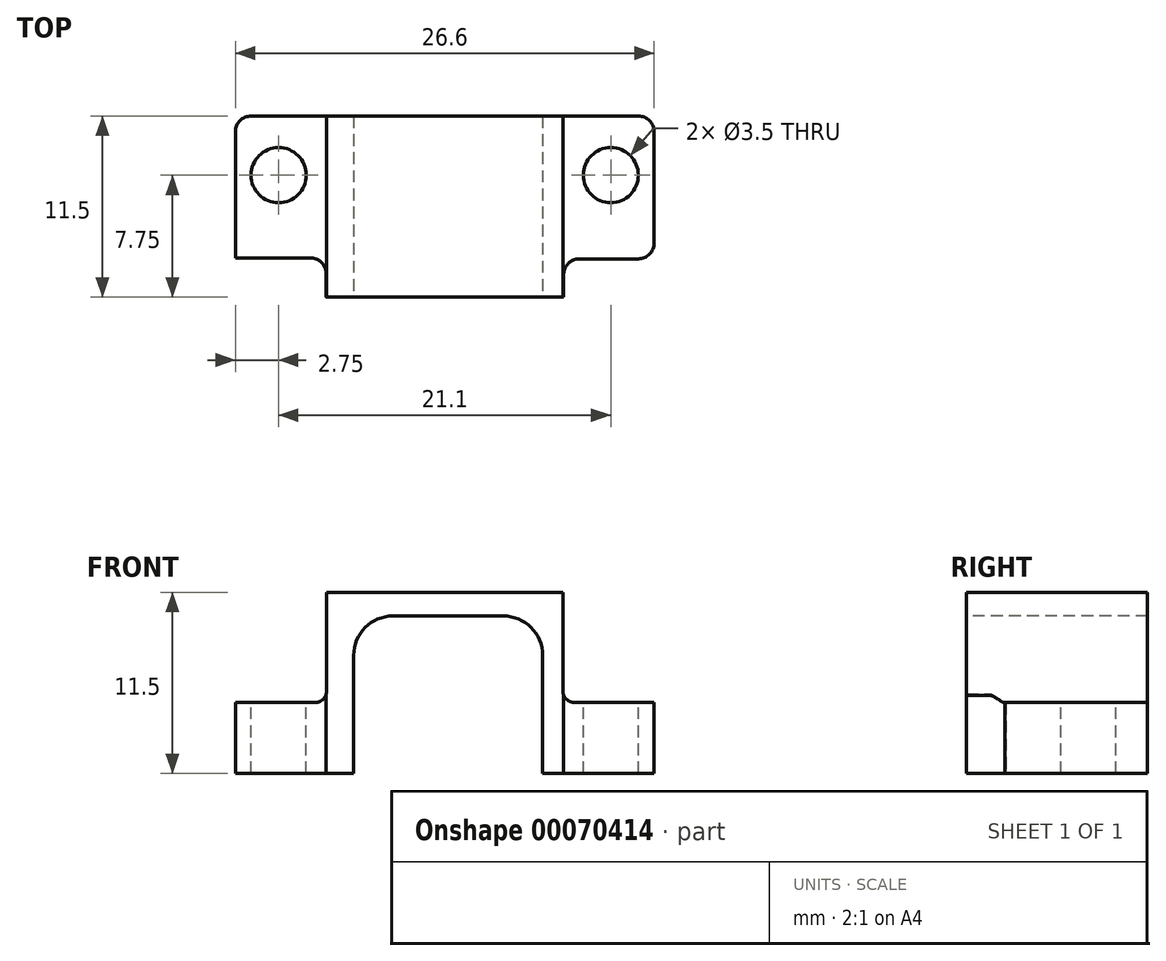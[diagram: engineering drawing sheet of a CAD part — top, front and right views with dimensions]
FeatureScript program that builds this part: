
annotation { "Feature Type Name" : "Feature", "Feature Type Description" : "" }
export const myFeature = defineFeature(function(context is Context, id is Id, definition is map)
    precondition{}
    {
        {
            var Q0;
            Q0=qCreatedBy(makeId("Top.planeOp"),FACE);
            var sketch = newSketch(context, id + "F0", { "sketchPlane" : qUnion([Q0])});
            skLineSegment(sketch, "E0.rect.bottom", {"start": v(-13.3, 5.75) * mm, "end": v(13.3, 5.75) * mm});
            skLineSegment(sketch, "E0.rect.top", {"start": v(-13.3, -5.75) * mm, "end": v(13.3, -5.75) * mm});
            skLineSegment(sketch, "E0.rect.left", {"start": v(-13.3, 5.75) * mm, "end": v(-13.3, -5.75) * mm});
            skLineSegment(sketch, "E0.rect.right", {"start": v(13.3, 5.75) * mm, "end": v(13.3, -5.75) * mm});
            skPoint(sketch, "E0.rect.middle", {"position": v(0, 0) * mm});
            skSolve(sketch);
        }
        {
            var Q0;
            Q0 = qSketchRegion(id + "F0", true);
            extrude(context, id + "F1", {"entities" : qUnion([Q0]), "endBound" : BoundingType.SYMMETRIC, "depth" : 11.5 * mm});
        }
        {
            var Q0;
            Q0=makeQuery(id+"F1.opExtrude","SWEPT_FACE",FACE,{"disambiguationData":[OSD([sQuery(id+"F0.wireOp",EDGE,"E0.rect.top")])]});
            var sketch = newSketch(context, id + "F2", { "sketchPlane" : qUnion([Q0])});
            skLineSegment(sketch, "E1", {"start": v(-5.78, -5.75) * mm, "end": v(-5.78, 4.25) * mm});
            skLineSegment(sketch, "E2", {"start": v(-5.78, 4.25) * mm, "end": v(6.22, 4.25) * mm});
            skLineSegment(sketch, "E3", {"start": v(6.22, 4.25) * mm, "end": v(6.22, -5.75) * mm});
            skLineSegment(sketch, "E4", {"start": v(6.22, -5.75) * mm, "end": v(-5.78, -5.75) * mm});
            skLineSegment(sketch, "E5", {"start": v(-7.5, 5.75) * mm, "end": v(-7.5, -1.25) * mm});
            skLineSegment(sketch, "E6", {"start": v(-7.5, -1.25) * mm, "end": v(-13.3, -1.25) * mm});
            skLineSegment(sketch, "E7", {"start": v(7.5, 5.75) * mm, "end": v(7.5, -1.25) * mm});
            skLineSegment(sketch, "E8", {"start": v(7.5, -1.25) * mm, "end": v(13.3, -1.25) * mm});
            skLineSegment(sketch, "E9", {"start": v(-7.5, 5.75) * mm, "end": v(-13.3, 5.75) * mm});
            skLineSegment(sketch, "E10", {"start": v(-13.3, 5.75) * mm, "end": v(-13.3, -1.25) * mm});
            skLineSegment(sketch, "E11", {"start": v(7.5, 5.75) * mm, "end": v(13.3, 5.75) * mm});
            skLineSegment(sketch, "E12", {"start": v(13.3, 5.75) * mm, "end": v(13.3, -1.25) * mm});
            skSolve(sketch);
        }
        {
            var Q0;
            Q0=makeQuery(id+"F2.imprint","IMPRINT",FACE,{"disambiguationData":[TD([[makeQuery(id+"F2.imprint","IMPRINT",EDGE,{"derivedFrom":sQuery(id+"F2.wireOp",EDGE,"E1")}),-1.0]])]});
            var Q1;
            Q1=makeQuery(id+"F2.imprint","IMPRINT",FACE,{"disambiguationData":[TD([[makeQuery(id+"F2.imprint","IMPRINT",EDGE,{"derivedFrom":sQuery(id+"F2.wireOp",EDGE,"E7")}),1.0]])]});
            var Q2;
            Q2=makeQuery(id+"F2.imprint","IMPRINT",FACE,{"disambiguationData":[TD([[makeQuery(id+"F2.imprint","IMPRINT",EDGE,{"derivedFrom":sQuery(id+"F2.wireOp",EDGE,"E5")}),-1.0]])]});
            extrude(context, id + "F3", {"entities" : qUnion([Q0, Q1, Q2]), "operationType" : NewBodyOperationType.REMOVE, "endBound" : BoundingType.THROUGH_ALL, "oppositeDirection" : true, "depth" : 25 * mm});
        }
        {
            var Q0;
            Q0=makeQuery(id+"F0.imprint","IMPRINT",FACE,{"disambiguationData":[TD([[makeQuery(id+"F0.imprint","IMPRINT",EDGE,{"derivedFrom":sQuery(id+"F0.wireOp",EDGE,"E0.rect.bottom")}),-1.0]])]});
            var sketch = newSketch(context, id + "F4", { "sketchPlane" : qUnion([Q0])});
            skCircle(sketch, "E13", {"center": v(-10.55, 2) * mm, "radius": 1.75 * mm});
            skCircle(sketch, "E14", {"center": v(10.55, 2) * mm, "radius": 1.75 * mm});
            skLineSegment(sketch, "E15", {"start": v(-7.53, -3.26) * mm, "end": v(-13.3, -3.26) * mm});
            skLineSegment(sketch, "E16", {"start": v(-13.3, -3.26) * mm, "end": v(-13.3, -5.76) * mm});
            skLineSegment(sketch, "E17", {"start": v(-7.53, -3.26) * mm, "end": v(-7.53, -5.76) * mm});
            skLineSegment(sketch, "E18", {"start": v(-13.3, -5.76) * mm, "end": v(-7.53, -5.76) * mm});
            skLineSegment(sketch, "E19", {"start": v(13.66, -3.31) * mm, "end": v(7.56, -3.31) * mm});
            skLineSegment(sketch, "E20", {"start": v(13.66, -3.31) * mm, "end": v(13.66, -5.81) * mm});
            skLineSegment(sketch, "E21", {"start": v(7.56, -5.81) * mm, "end": v(13.66, -5.81) * mm});
            skLineSegment(sketch, "E22", {"start": v(7.56, -3.31) * mm, "end": v(7.56, -5.81) * mm});
            skSolve(sketch);
        }
        {
            var Q0;
            Q0 = qSketchRegion(id + "F4", true);
            extrude(context, id + "F5", {"entities" : qUnion([Q0]), "operationType" : NewBodyOperationType.REMOVE, "endBound" : BoundingType.THROUGH_ALL, "oppositeDirection" : true, "depth" : 25 * mm});
        }
        {
            var Q0;
            Q0=makeQuery(id+"F5.boolean.opBoolean","COPY",EDGE,{"derivedFrom":makeQuery(id+"F5.opExtrude","SWEPT_EDGE",EDGE,{"disambiguationData":[OSD([sQuery(id+"F4.wireOp",EDGE,"E15"),sQuery(id+"F4.wireOp",EDGE,"E17")])]})});
            var Q1;
            Q1=makeQuery(id+"F5.boolean.opBoolean","COPY",EDGE,{"derivedFrom":makeQuery(id+"F5.opExtrude","SWEPT_EDGE",EDGE,{"disambiguationData":[OSD([sQuery(id+"F4.wireOp",EDGE,"E15"),sQuery(id+"F4.wireOp",EDGE,"E16")])]})});
            var Q2;
            Q2=makeQuery(id+"F1.opExtrude","SWEPT_EDGE",EDGE,{"disambiguationData":[OSD([sQuery(id+"F0.wireOp",EDGE,"E0.rect.bottom"),sQuery(id+"F0.wireOp",EDGE,"E0.rect.left")])]});
            var Q3;
            Q3=makeQuery(id+"F1.opExtrude","SWEPT_EDGE",EDGE,{"disambiguationData":[OSD([sQuery(id+"F0.wireOp",EDGE,"E0.rect.bottom"),sQuery(id+"F0.wireOp",EDGE,"E0.rect.right")])]});
            var Q4;
            Q4=makeQuery(id+"F5.boolean.opBoolean","INTERSECT",EDGE,{"derivedFrom":[makeQuery(id+"F1.opExtrude","SWEPT_FACE",FACE,{"disambiguationData":[OSD([sQuery(id+"F0.wireOp",EDGE,"E0.rect.right")])]}),makeQuery(id+"F5.opExtrude","SWEPT_FACE",FACE,{"disambiguationData":[OSD([sQuery(id+"F4.wireOp",EDGE,"E19")])]})]});
            var Q5;
            Q5=makeQuery(id+"F5.boolean.opBoolean","COPY",EDGE,{"derivedFrom":makeQuery(id+"F5.opExtrude","SWEPT_EDGE",EDGE,{"disambiguationData":[OSD([sQuery(id+"F4.wireOp",EDGE,"E19"),sQuery(id+"F4.wireOp",EDGE,"E22")])]})});
            fillet(context, id + "F6", {"entities" : qUnion([Q0, Q1, Q2, Q3, Q4, Q5]), "radius" : 1 * mm, "tangentPropagation" : true, "allowEdgeOverflow" : false});
        }
        {
            var Q0;
            Q0=makeQuery(id+"F3.boolean.opBoolean","COPY",EDGE,{"derivedFrom":makeQuery(id+"F3.opExtrude","SWEPT_EDGE",EDGE,{"disambiguationData":[OSD([sQuery(id+"F2.wireOp",EDGE,"E7"),sQuery(id+"F2.wireOp",EDGE,"E8")])]})});
            var Q1;
            Q1=makeQuery(id+"F3.boolean.opBoolean","COPY",EDGE,{"derivedFrom":makeQuery(id+"F3.opExtrude","SWEPT_EDGE",EDGE,{"disambiguationData":[OSD([sQuery(id+"F2.wireOp",EDGE,"E5"),sQuery(id+"F2.wireOp",EDGE,"E6")])]})});
            fillet(context, id + "F7", {"entities" : qUnion([Q0, Q1]), "radius" : .75 * mm, "tangentPropagation" : true, "allowEdgeOverflow" : false});
        }
        {
            var Q0;
            Q0=makeQuery(id+"F3.boolean.opBoolean","COPY",EDGE,{"derivedFrom":makeQuery(id+"F3.opExtrude","SWEPT_EDGE",EDGE,{"disambiguationData":[OSD([sQuery(id+"F2.wireOp",EDGE,"E2"),sQuery(id+"F2.wireOp",EDGE,"E3")])]})});
            var Q1;
            Q1=makeQuery(id+"F3.boolean.opBoolean","COPY",EDGE,{"derivedFrom":makeQuery(id+"F3.opExtrude","SWEPT_EDGE",EDGE,{"disambiguationData":[OSD([sQuery(id+"F2.wireOp",EDGE,"E1"),sQuery(id+"F2.wireOp",EDGE,"E2")])]})});
            fillet(context, id + "F8", {"entities" : qUnion([Q0, Q1]), "radius" : 2.5 * mm, "tangentPropagation" : true, "allowEdgeOverflow" : false});
        }
    });
